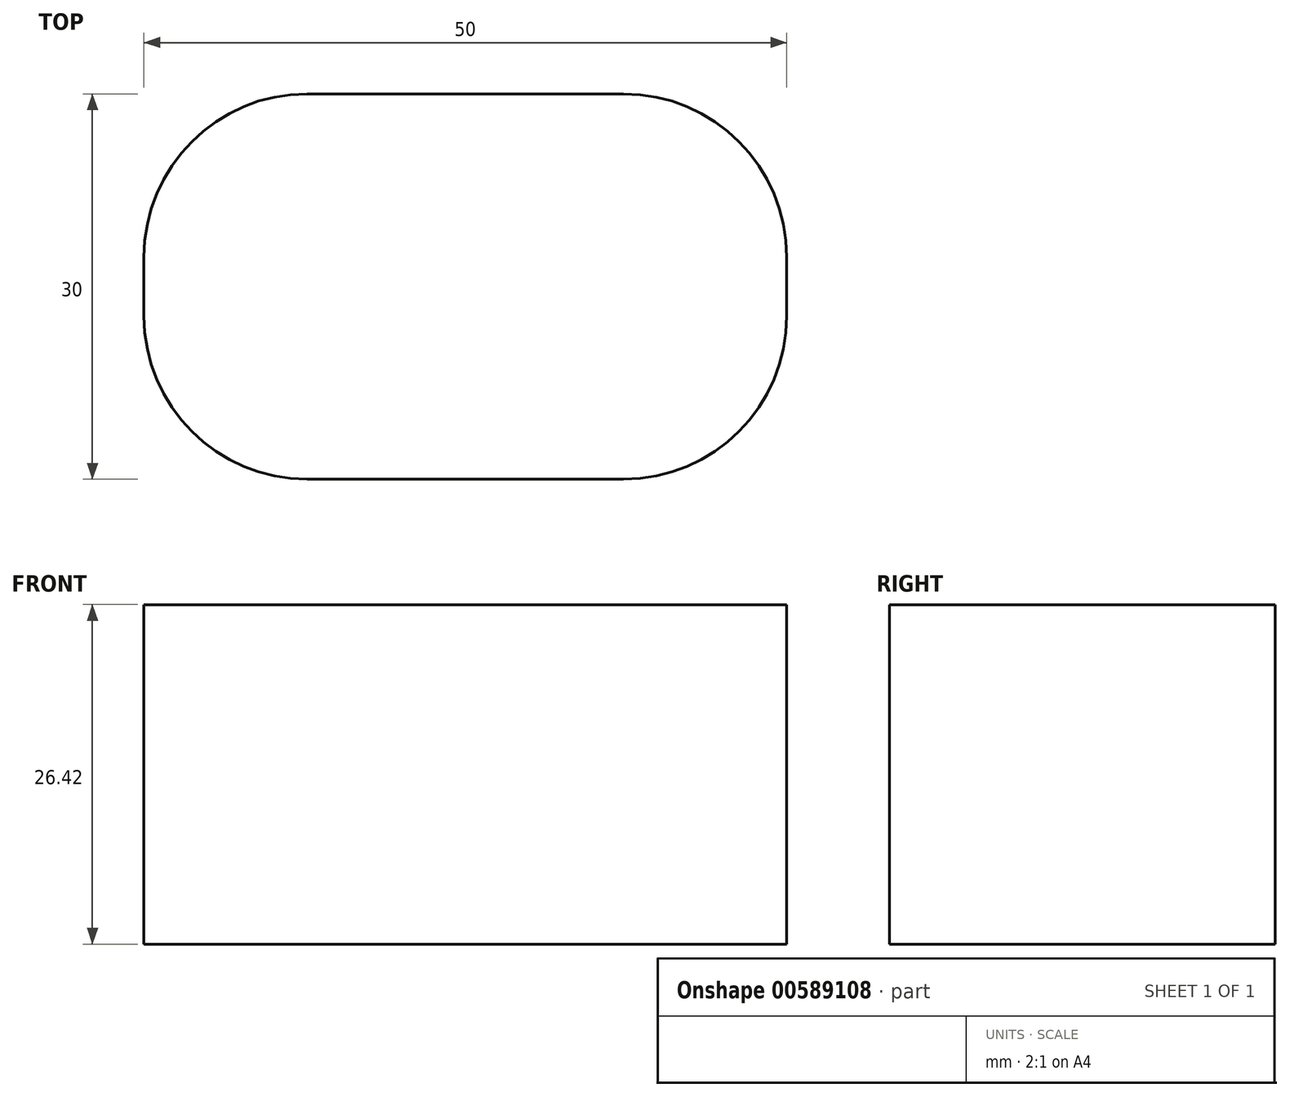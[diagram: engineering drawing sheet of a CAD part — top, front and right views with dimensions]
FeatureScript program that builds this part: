
annotation { "Feature Type Name" : "Feature", "Feature Type Description" : "" }
export const myFeature = defineFeature(function(context is Context, id is Id, definition is map)
    precondition{}
    {
        {
            var Q0;
            Q0=qCreatedBy(makeId("Top.planeOp"),FACE);
            var sketch = newSketch(context, id + "F0", { "sketchPlane" : qUnion([Q0])});
            skLineSegment(sketch, "E0.bottom", {"start": v(25, 15) * mm, "end": v(-25, 15) * mm});
            skLineSegment(sketch, "E0.top", {"start": v(25, -15) * mm, "end": v(-25, -15) * mm});
            skLineSegment(sketch, "E0.left", {"start": v(25, 15) * mm, "end": v(25, -15) * mm});
            skLineSegment(sketch, "E0.right", {"start": v(-25, 15) * mm, "end": v(-25, -15) * mm});
            skPoint(sketch, "E0.middle", {"position": v(0, 0) * mm});
            skSolve(sketch);
        }
        {
            var Q0;
            Q0 = qSketchRegion(id + "F0", true);
            extrude(context, id + "F1", {"entities" : qUnion([Q0]), "depth" : 26.42 * mm, "offsetDistance" : 25.4 * mm});
        }
        {
            var Q0;
            Q0=makeQuery(id+"F1.opExtrude","SWEPT_EDGE",EDGE,{"disambiguationData":[OSD([sQuery(id+"F0.wireOp",EDGE,"E0.top"),sQuery(id+"F0.wireOp",EDGE,"E0.left")])]});
            var Q1;
            Q1=makeQuery(id+"F1.opExtrude","SWEPT_EDGE",EDGE,{"disambiguationData":[OSD([sQuery(id+"F0.wireOp",EDGE,"E0.bottom"),sQuery(id+"F0.wireOp",EDGE,"E0.left")])]});
            var Q2;
            Q2=makeQuery(id+"F1.opExtrude","SWEPT_EDGE",EDGE,{"disambiguationData":[OSD([sQuery(id+"F0.wireOp",EDGE,"E0.top"),sQuery(id+"F0.wireOp",EDGE,"E0.right")])]});
            var Q3;
            Q3=makeQuery(id+"F1.opExtrude","SWEPT_EDGE",EDGE,{"disambiguationData":[OSD([sQuery(id+"F0.wireOp",EDGE,"E0.bottom"),sQuery(id+"F0.wireOp",EDGE,"E0.right")])]});
            fillet(context, id + "F2", {"entities" : qUnion([Q0, Q1, Q2, Q3]), "radius" : 12.7 * mm, "tangentPropagation" : true, "allowEdgeOverflow" : false});
        }
    });
